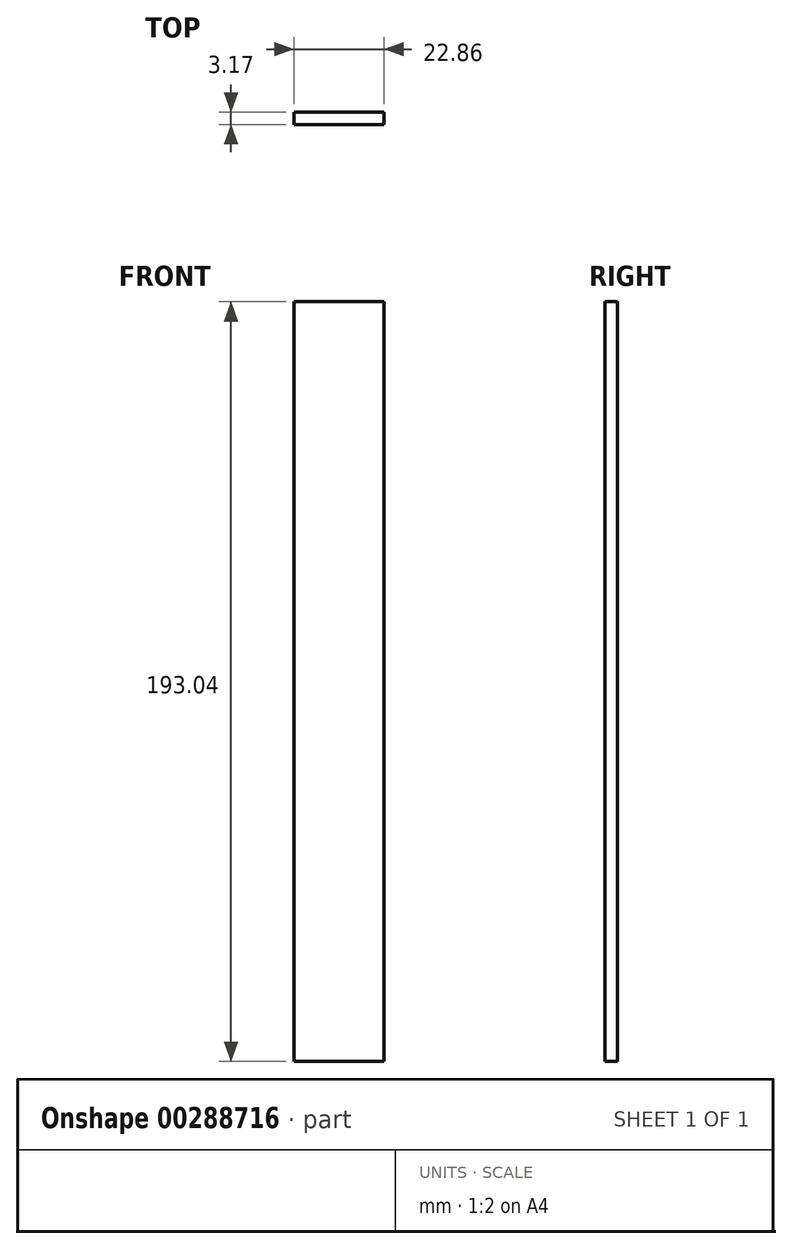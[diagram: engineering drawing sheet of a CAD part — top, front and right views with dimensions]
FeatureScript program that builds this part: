
annotation { "Feature Type Name" : "Feature", "Feature Type Description" : "" }
export const myFeature = defineFeature(function(context is Context, id is Id, definition is map)
    precondition{}
    {
        {
            var Q0;
            Q0=qCreatedBy(makeId("Front.planeOp"),FACE);
            var sketch = newSketch(context, id + "F0", { "sketchPlane" : qUnion([Q0])});
            skLineSegment(sketch, "E0.bottom", {"start": v(11.43, -96.52) * mm, "end": v(-11.43, -96.52) * mm});
            skLineSegment(sketch, "E0.top", {"start": v(11.43, 96.52) * mm, "end": v(-11.43, 96.52) * mm});
            skLineSegment(sketch, "E0.left", {"start": v(11.43, -96.52) * mm, "end": v(11.43, 96.52) * mm});
            skLineSegment(sketch, "E0.right", {"start": v(-11.43, -96.52) * mm, "end": v(-11.43, 96.52) * mm});
            skPoint(sketch, "E0.middle", {"position": v(0, 0) * mm});
            skSolve(sketch);
        }
        {
            var Q0;
            Q0=makeQuery(id+"F0.imprint","IMPRINT",FACE,{"disambiguationData":[TD([[makeQuery(id+"F0.imprint","IMPRINT",EDGE,{"derivedFrom":sQuery(id+"F0.wireOp",EDGE,"E0.bottom")}),-1.0]])]});
            extrude(context, id + "F1", {"entities" : qUnion([Q0]), "depth" : 3.17 * mm});
        }
    });
